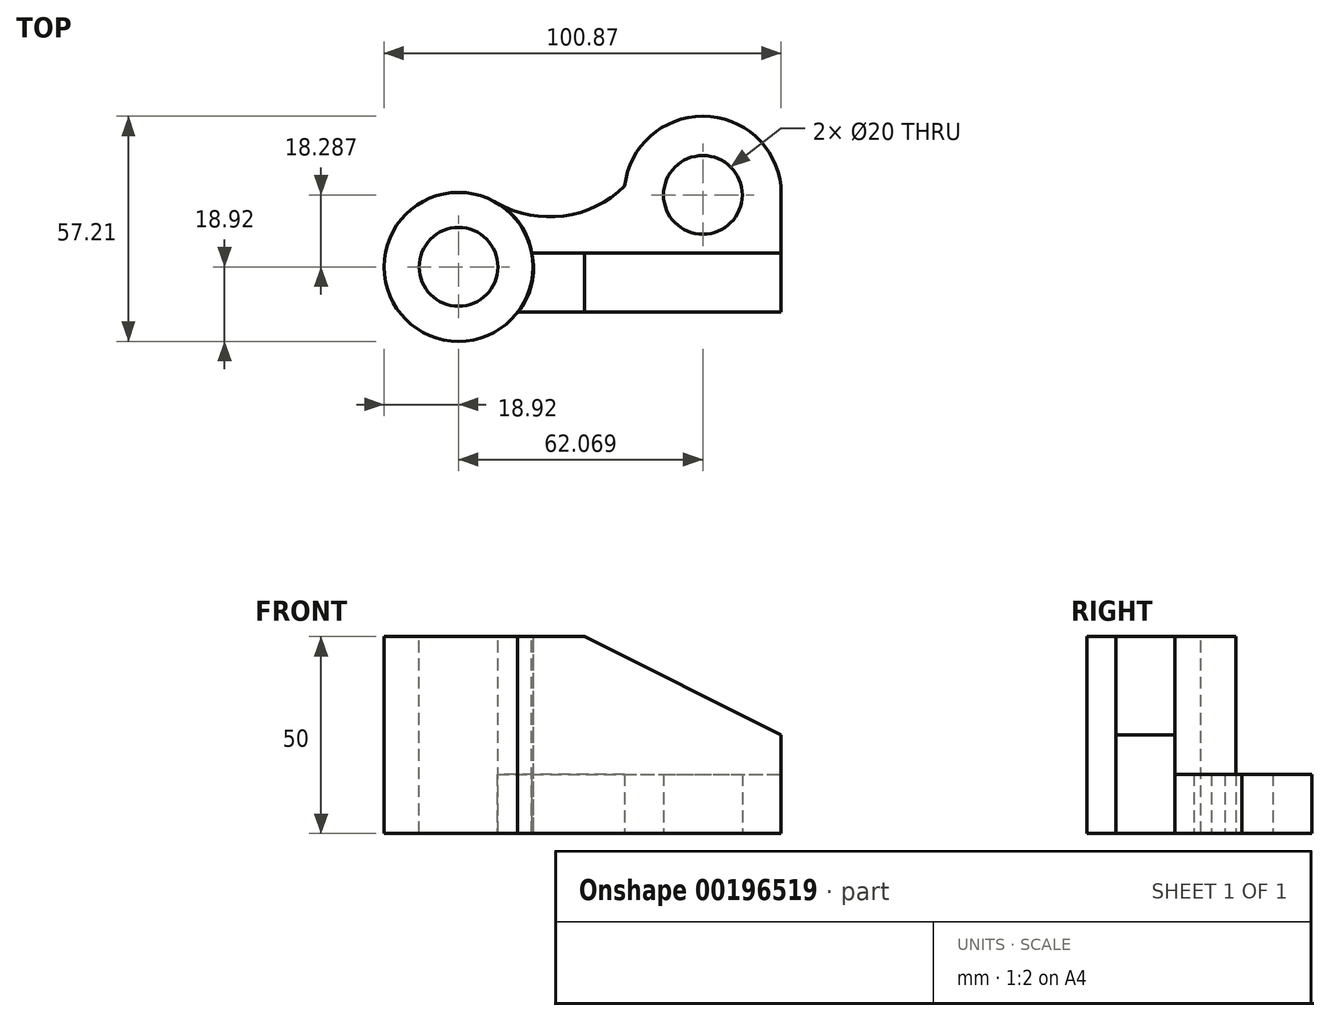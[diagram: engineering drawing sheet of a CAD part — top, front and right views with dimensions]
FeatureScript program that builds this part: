
annotation { "Feature Type Name" : "Feature", "Feature Type Description" : "" }
export const myFeature = defineFeature(function(context is Context, id is Id, definition is map)
    precondition{}
    {
        {
            var Q0;
            Q0=qCreatedBy(makeId("Front.planeOp"),FACE);
            var sketch = newSketch(context, id + "F0", { "sketchPlane" : qUnion([Q0])});
            skLineSegment(sketch, "E0.bottom", {"start": v(0, 0) * mm, "end": v(18.92, 0) * mm});
            skLineSegment(sketch, "E0.top", {"start": v(0, 50) * mm, "end": v(18.92, 50) * mm});
            skLineSegment(sketch, "E0.left", {"start": v(0, 0) * mm, "end": v(0, 50) * mm});
            skLineSegment(sketch, "E0.right", {"start": v(18.92, 0) * mm, "end": v(18.92, 50) * mm});
            skSolve(sketch);
        }
        {
            var Q0;
            Q0 = qSketchRegion(id + "F0", true);
            var Q1;
            Q1=sQuery(id+"F0.wireOp",EDGE,"E0.left");
            revolve(context, id + "F1", {"entities" : qUnion([Q0]), "axis" : qUnion([Q1]), "revolveType" : RevolveType.FULL});
        }
        {
            var Q0;
            Q0=makeQuery(id+"F1.opRevolve","SWEPT_FACE",FACE,{"disambiguationData":[OSD([sQuery(id+"F0.wireOp",EDGE,"E0.top")])]});
            var sketch = newSketch(context, id + "F2", { "sketchPlane" : qUnion([Q0])});
            skCircle(sketch, "E1", {"center": v(0, 0) * mm, "radius": 10 * mm});
            skSolve(sketch);
        }
        {
            var Q0;
            Q0 = qSketchRegion(id + "F2", true);
            extrude(context, id + "F3", {"entities" : qUnion([Q0]), "operationType" : NewBodyOperationType.REMOVE, "oppositeDirection" : true, "depth" : 50 * mm});
        }
        {
            var Q0;
            Q0=makeQuery(id+"F1.opRevolve","SWEPT_FACE",FACE,{"disambiguationData":[OSD([sQuery(id+"F0.wireOp",EDGE,"E0.top")])]});
            var sketch = newSketch(context, id + "F4", { "sketchPlane" : qUnion([Q0])});
            skLineSegment(sketch, "E2.bottom", {"start": v(18.6, 3.48) * mm, "end": v(81.95, 3.48) * mm});
            skLineSegment(sketch, "E2.top", {"start": v(15.01, -11.52) * mm, "end": v(81.95, -11.52) * mm});
            skLineSegment(sketch, "E2.right", {"start": v(81.95, 3.48) * mm, "end": v(81.95, -11.52) * mm});
            skArc(sketch, "E3", {"start": v(15.01, -11.52) * mm, "mid": v(18.56, -4.43) * mm, "end": v(18.6, 3.48) * mm});
            skSolve(sketch);
        }
        {
            var Q0;
            Q0 = qSketchRegion(id + "F4", true);
            extrude(context, id + "F5", {"entities" : qUnion([Q0]), "oppositeDirection" : true, "depth" : 50 * mm});
        }
        {
            var Q0;
            Q0=makeQuery(id+"F5.opExtrude","SWEPT_FACE",FACE,{"disambiguationData":[OSD([sQuery(id+"F4.wireOp",EDGE,"E2.bottom")])]});
            var sketch = newSketch(context, id + "F6", { "sketchPlane" : qUnion([Q0])});
            skLineSegment(sketch, "E4", {"start": v(-31.95, 50) * mm, "end": v(-81.95, 25) * mm});
            skLineSegment(sketch, "E5", {"start": v(-81.95, 0) * mm, "end": v(-71.8, 0) * mm, "construction": true});
            skLineSegment(sketch, "E6", {"start": v(-31.95, 50) * mm, "end": v(-81.95, 50) * mm});
            skLineSegment(sketch, "E7", {"start": v(-81.95, 50) * mm, "end": v(-81.95, 25) * mm});
            skSolve(sketch);
        }
        {
            var Q0;
            Q0 = qSketchRegion(id + "F6", true);
            extrude(context, id + "F7", {"entities" : qUnion([Q0]), "operationType" : NewBodyOperationType.REMOVE, "oppositeDirection" : true, "depth" : 15 * mm});
        }
        {
            var Q0;
            Q0=makeQuery(id+"F5.opExtrude","CAP_FACE",FACE,{"disambiguationData":[OSD([sQuery(id+"F4.wireOp",EDGE,"E2.bottom"),sQuery(id+"F4.wireOp",EDGE,"E2.top"),sQuery(id+"F4.wireOp",EDGE,"E2.right"),sQuery(id+"F4.wireOp",EDGE,"E3")])],"isStart":false});
            var sketch = newSketch(context, id + "F8", { "sketchPlane" : qUnion([Q0])});
            skArc(sketch, "E8", {"start": v(9.8, -16.18) * mm, "mid": v(15.67, -10.85) * mm, "end": v(18.6, -3.48) * mm});
            skArc(sketch, "E9", {"start": v(42.2, -20.48) * mm, "mid": v(62.07, -38.29) * mm, "end": v(81.95, -20.48) * mm});
            skArc(sketch, "E10", {"start": v(42.2, -20.48) * mm, "mid": v(26.71, -12.95) * mm, "end": v(9.8, -16.18) * mm});
            skLineSegment(sketch, "E11", {"start": v(81.95, -3.48) * mm, "end": v(81.95, -20.48) * mm});
            skLineSegment(sketch, "E12", {"start": v(81.95, -3.48) * mm, "end": v(18.6, -3.48) * mm});
            skSolve(sketch);
        }
        {
            var Q0;
            Q0 = qSketchRegion(id + "F8", true);
            extrude(context, id + "F9", {"entities" : qUnion([Q0]), "oppositeDirection" : true, "depth" : 15 * mm});
        }
        {
            var Q0;
            Q0=makeQuery(id+"F9.opExtrude","CAP_FACE",FACE,{"disambiguationData":[OSD([sQuery(id+"F8.wireOp",EDGE,"E8"),sQuery(id+"F8.wireOp",EDGE,"E9"),sQuery(id+"F8.wireOp",EDGE,"E10"),sQuery(id+"F8.wireOp",EDGE,"E11"),sQuery(id+"F8.wireOp",EDGE,"E12")])],"isStart":true});
            var sketch = newSketch(context, id + "F10", { "sketchPlane" : qUnion([Q0])});
            skCircle(sketch, "E13", {"center": v(62.07, -18.29) * mm, "radius": 10 * mm});
            skSolve(sketch);
        }
        {
            var Q0;
            Q0 = qSketchRegion(id + "F10", true);
            extrude(context, id + "F11", {"entities" : qUnion([Q0]), "operationType" : NewBodyOperationType.REMOVE, "oppositeDirection" : true, "depth" : 15 * mm});
        }
    });
